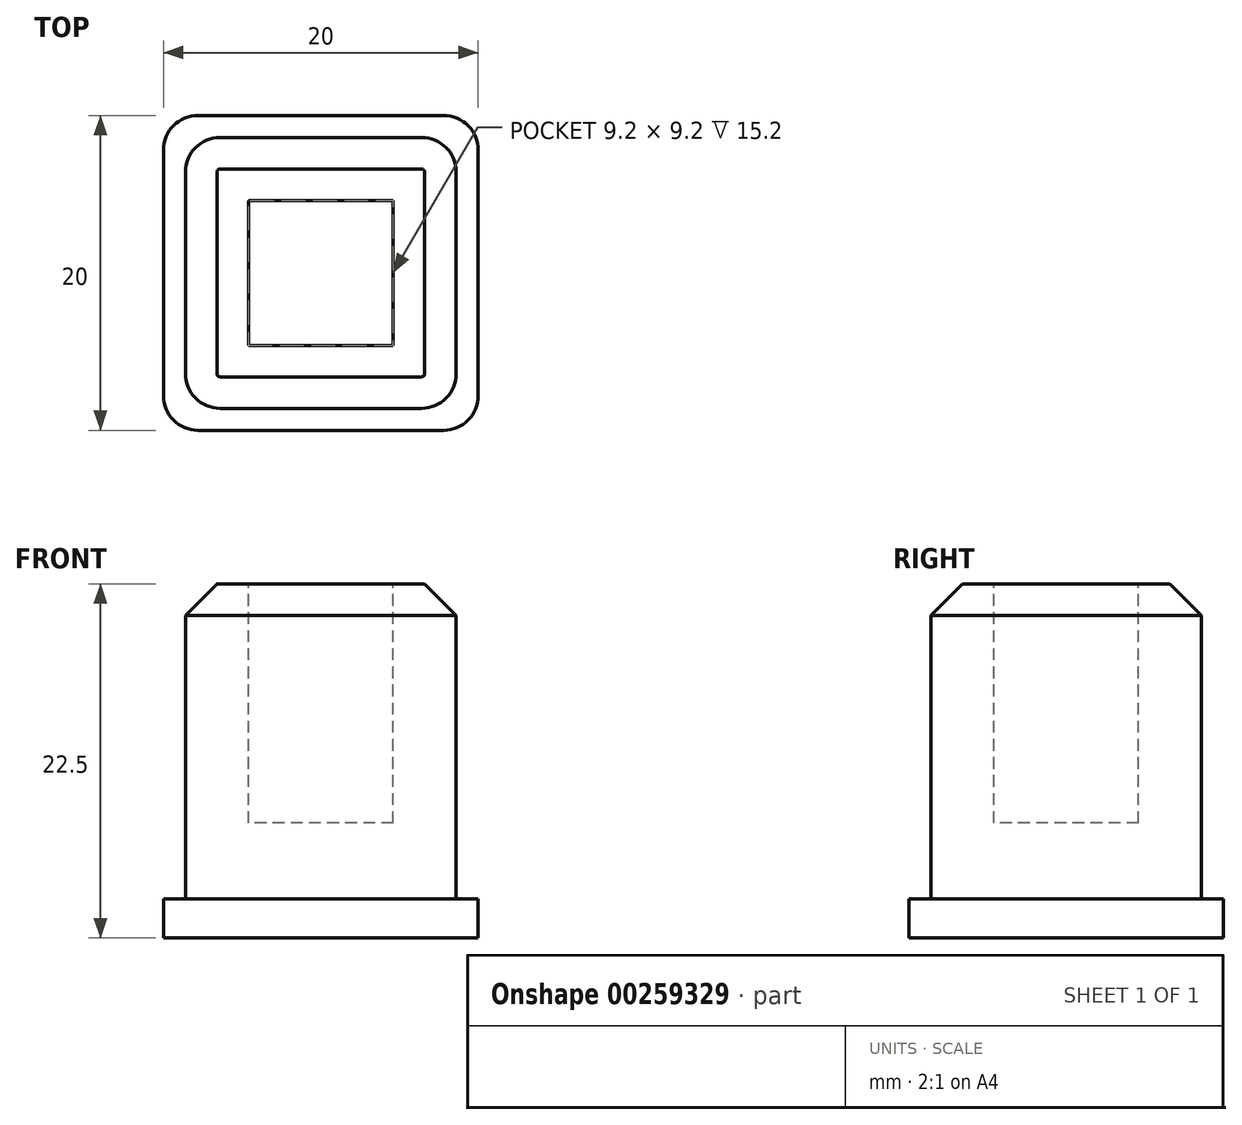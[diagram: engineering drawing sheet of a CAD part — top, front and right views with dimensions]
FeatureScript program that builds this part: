
annotation { "Feature Type Name" : "Feature", "Feature Type Description" : "" }
export const myFeature = defineFeature(function(context is Context, id is Id, definition is map)
    precondition{}
    {
        {
            var Q0;
            Q0=qCreatedBy(makeId("Top.planeOp"),FACE);
            var sketch = newSketch(context, id + "F0", { "sketchPlane" : qUnion([Q0])});
            skLineSegment(sketch, "E0.bottom", {"start": v(-10, 10) * mm, "end": v(10, 10) * mm});
            skLineSegment(sketch, "E0.top", {"start": v(-10, -10) * mm, "end": v(10, -10) * mm});
            skLineSegment(sketch, "E0.left", {"start": v(-10, 10) * mm, "end": v(-10, -10) * mm});
            skLineSegment(sketch, "E0.right", {"start": v(10, 10) * mm, "end": v(10, -10) * mm});
            skSolve(sketch);
        }
        {
            var Q0;
            Q0=makeQuery(id+"F0.imprint","IMPRINT",FACE,{"disambiguationData":[TD([[makeQuery(id+"F0.imprint","IMPRINT",EDGE,{"derivedFrom":sQuery(id+"F0.wireOp",EDGE,"E0.bottom")}),-1.0]])]});
            extrude(context, id + "F1", {"entities" : qUnion([Q0]), "depth" : 2.5 * mm, "offsetDistance" : 25 * mm});
        }
        {
            var Q0;
            Q0=makeQuery(id+"F1.opExtrude","CAP_FACE",FACE,{"disambiguationData":[OSD([sQuery(id+"F0.wireOp",EDGE,"E0.bottom"),sQuery(id+"F0.wireOp",EDGE,"E0.top"),sQuery(id+"F0.wireOp",EDGE,"E0.left"),sQuery(id+"F0.wireOp",EDGE,"E0.right")])],"isStart":false});
            var sketch = newSketch(context, id + "F2", { "sketchPlane" : qUnion([Q0])});
            skLineSegment(sketch, "E1.bottom", {"start": v(-8.6, 8.6) * mm, "end": v(8.6, 8.6) * mm});
            skLineSegment(sketch, "E1.top", {"start": v(-8.6, -8.6) * mm, "end": v(8.6, -8.6) * mm});
            skLineSegment(sketch, "E1.left", {"start": v(-8.6, 8.6) * mm, "end": v(-8.6, -8.6) * mm});
            skLineSegment(sketch, "E1.right", {"start": v(8.6, 8.6) * mm, "end": v(8.6, -8.6) * mm});
            skSolve(sketch);
        }
        {
            var Q0;
            Q0=makeQuery(id+"F2.imprint","IMPRINT",FACE,{"disambiguationData":[TD([[makeQuery(id+"F2.imprint","IMPRINT",EDGE,{"derivedFrom":sQuery(id+"F2.wireOp",EDGE,"E1.bottom")}),-1.0]])]});
            extrude(context, id + "F3", {"entities" : qUnion([Q0]), "operationType" : NewBodyOperationType.ADD, "depth" : 20 * mm, "offsetDistance" : 25 * mm});
        }
        {
            var Q0;
            Q0=makeQuery(id+"F3.opExtrude","SWEPT_EDGE",EDGE,{"disambiguationData":[OSD([sQuery(id+"F2.wireOp",EDGE,"E1.top"),sQuery(id+"F2.wireOp",EDGE,"E1.left")])]});
            var Q1;
            Q1=makeQuery(id+"F3.opExtrude","SWEPT_EDGE",EDGE,{"disambiguationData":[OSD([sQuery(id+"F2.wireOp",EDGE,"E1.bottom"),sQuery(id+"F2.wireOp",EDGE,"E1.left")])]});
            var Q2;
            Q2=makeQuery(id+"F3.opExtrude","SWEPT_EDGE",EDGE,{"disambiguationData":[OSD([sQuery(id+"F2.wireOp",EDGE,"E1.bottom"),sQuery(id+"F2.wireOp",EDGE,"E1.right")])]});
            var Q3;
            Q3=makeQuery(id+"F3.opExtrude","SWEPT_EDGE",EDGE,{"disambiguationData":[OSD([sQuery(id+"F2.wireOp",EDGE,"E1.top"),sQuery(id+"F2.wireOp",EDGE,"E1.right")])]});
            var Q4;
            Q4=makeQuery(id+"F1.opExtrude","SWEPT_EDGE",EDGE,{"disambiguationData":[OSD([sQuery(id+"F0.wireOp",EDGE,"E0.top"),sQuery(id+"F0.wireOp",EDGE,"E0.right")])]});
            var Q5;
            Q5=makeQuery(id+"F1.opExtrude","SWEPT_EDGE",EDGE,{"disambiguationData":[OSD([sQuery(id+"F0.wireOp",EDGE,"E0.bottom"),sQuery(id+"F0.wireOp",EDGE,"E0.right")])]});
            var Q6;
            Q6=makeQuery(id+"F1.opExtrude","SWEPT_EDGE",EDGE,{"disambiguationData":[OSD([sQuery(id+"F0.wireOp",EDGE,"E0.top"),sQuery(id+"F0.wireOp",EDGE,"E0.left")])]});
            var Q7;
            Q7=makeQuery(id+"F1.opExtrude","SWEPT_EDGE",EDGE,{"disambiguationData":[OSD([sQuery(id+"F0.wireOp",EDGE,"E0.bottom"),sQuery(id+"F0.wireOp",EDGE,"E0.left")])]});
            fillet(context, id + "F4", {"entities" : qUnion([Q0, Q1, Q2, Q3, Q4, Q5, Q6, Q7]), "radius" : 2.2 * mm, "tangentPropagation" : true, "allowEdgeOverflow" : false});
        }
        {
            var Q0;
            Q0=makeQuery(id+"F3.opExtrude","CAP_FACE",FACE,{"disambiguationData":[OSD([sQuery(id+"F2.wireOp",EDGE,"E1.bottom"),sQuery(id+"F2.wireOp",EDGE,"E1.top"),sQuery(id+"F2.wireOp",EDGE,"E1.left"),sQuery(id+"F2.wireOp",EDGE,"E1.right")])],"isStart":false});
            var sketch = newSketch(context, id + "F5", { "sketchPlane" : qUnion([Q0])});
            skLineSegment(sketch, "E2.bottom", {"start": v(4.6, 4.6) * mm, "end": v(-4.6, 4.6) * mm});
            skLineSegment(sketch, "E2.top", {"start": v(4.6, -4.6) * mm, "end": v(-4.6, -4.6) * mm});
            skLineSegment(sketch, "E2.left", {"start": v(4.6, 4.6) * mm, "end": v(4.6, -4.6) * mm});
            skLineSegment(sketch, "E2.right", {"start": v(-4.6, 4.6) * mm, "end": v(-4.6, -4.6) * mm});
            skSolve(sketch);
        }
        {
            var Q0;
            Q0=makeQuery(id+"F5.imprint","IMPRINT",FACE,{"disambiguationData":[TD([[makeQuery(id+"F5.imprint","IMPRINT",EDGE,{"derivedFrom":sQuery(id+"F5.wireOp",EDGE,"E2.bottom")}),1.0]])]});
            extrude(context, id + "F6", {"entities" : qUnion([Q0]), "operationType" : NewBodyOperationType.REMOVE, "oppositeDirection" : true, "depth" : 15.2 * mm, "offsetDistance" : 25 * mm});
        }
        {
            var Q0;
            Q0=makeQuery(id+"F3.opExtrude","CAP_EDGE",EDGE,{"disambiguationData":[OSD([sQuery(id+"F2.wireOp",EDGE,"E1.bottom")])],"isStart":false});
            chamfer(context, id + "F7", {"entities" : qUnion([Q0]), "width" : 2 * mm, "tangentPropagation" : true});
        }
    });
